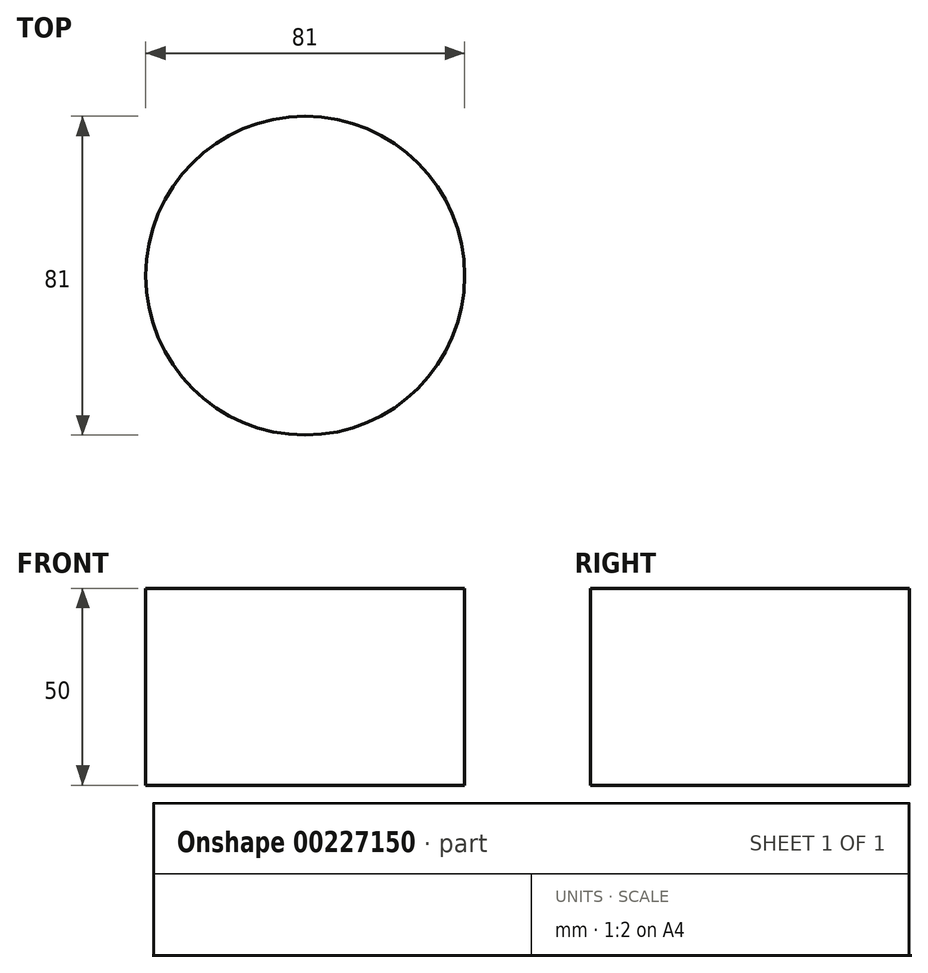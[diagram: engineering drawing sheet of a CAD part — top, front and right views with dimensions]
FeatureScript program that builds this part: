
annotation { "Feature Type Name" : "Feature", "Feature Type Description" : "" }
export const myFeature = defineFeature(function(context is Context, id is Id, definition is map)
    precondition{}
    {
        {
            var Q0;
            Q0=qCreatedBy(makeId("Top.planeOp"),FACE);
            var sketch = newSketch(context, id + "F0", { "sketchPlane" : qUnion([Q0])});
            skCircle(sketch, "E0", {"center": v(-1.31, 0) * mm, "radius": 40.5 * mm});
            skSolve(sketch);
        }
        {
            var Q0;
            Q0=makeQuery(id+"F0.imprint","IMPRINT",FACE,{"disambiguationData":[TD([[makeQuery(id+"F0.imprint","IMPRINT",EDGE,{"derivedFrom":sQuery(id+"F0.wireOp",EDGE,"E0")}),1.0]])]});
            extrude(context, id + "F1", {"entities" : qUnion([Q0]), "depth" : 50 * mm});
        }
    });
